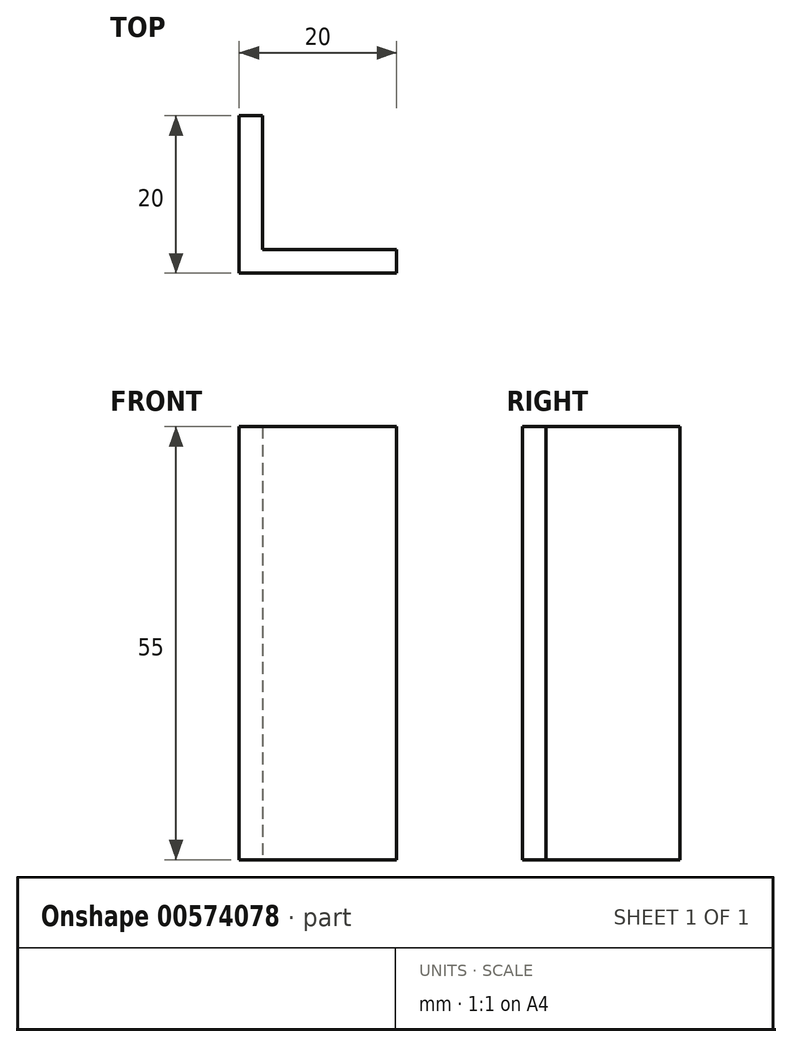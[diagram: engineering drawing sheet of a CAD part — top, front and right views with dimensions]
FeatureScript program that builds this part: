
annotation { "Feature Type Name" : "Feature", "Feature Type Description" : "" }
export const myFeature = defineFeature(function(context is Context, id is Id, definition is map)
    precondition{}
    {
        {
            var Q0;
            Q0=qCreatedBy(makeId("Top.planeOp"),FACE);
            var sketch = newSketch(context, id + "F0", { "sketchPlane" : qUnion([Q0])});
            skLineSegment(sketch, "E0.bottom", {"start": v(0, 0) * mm, "end": v(20, 0) * mm});
            skLineSegment(sketch, "E0.top", {"start": v(0, 20) * mm, "end": v(3, 20) * mm});
            skLineSegment(sketch, "E0.left", {"start": v(0, 0) * mm, "end": v(0, 20) * mm});
            skLineSegment(sketch, "E0.right", {"start": v(20, 0) * mm, "end": v(20, 3) * mm});
            skLineSegment(sketch, "E1.top", {"start": v(20, 3) * mm, "end": v(3, 3) * mm});
            skLineSegment(sketch, "E1.right", {"start": v(3, 20) * mm, "end": v(3, 3) * mm});
            skSolve(sketch);
        }
        {
            var Q0;
            Q0=makeQuery(id+"F0.imprint","IMPRINT",FACE,{"disambiguationData":[TD([[makeQuery(id+"F0.imprint","IMPRINT",EDGE,{"derivedFrom":sQuery(id+"F0.wireOp",EDGE,"E0.bottom")}),1.0]])]});
            extrude(context, id + "F1", {"entities" : qUnion([Q0]), "depth" : 55 * mm, "offsetDistance" : 25 * mm});
        }
    });
